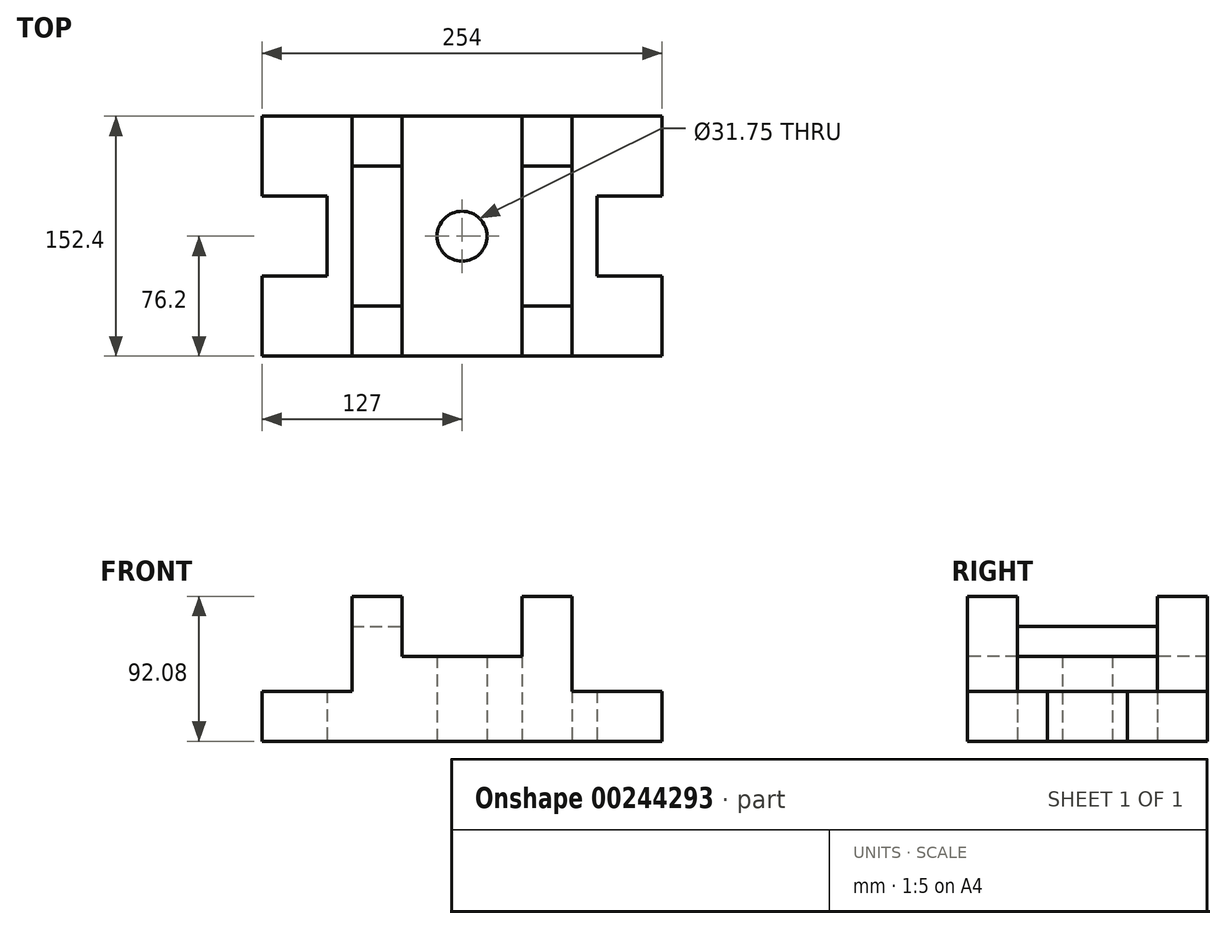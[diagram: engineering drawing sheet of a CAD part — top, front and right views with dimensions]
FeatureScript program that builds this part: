
annotation { "Feature Type Name" : "Feature", "Feature Type Description" : "" }
export const myFeature = defineFeature(function(context is Context, id is Id, definition is map)
    precondition{}
    {
        {
            var Q0;
            Q0=qCreatedBy(makeId("Top.planeOp"),FACE);
            var sketch = newSketch(context, id + "F0", { "sketchPlane" : qUnion([Q0])});
            skCircle(sketch, "E0", {"center": v(0, 0) * mm, "radius": 15.87 * mm});
            skLineSegment(sketch, "E1", {"start": v(0, 0) * mm, "end": v(0, 76.2) * mm});
            skLineSegment(sketch, "E2", {"start": v(0, 0) * mm, "end": v(0, -76.2) * mm});
            skLineSegment(sketch, "E3", {"start": v(0, 76.2) * mm, "end": v(38.1, 76.2) * mm});
            skLineSegment(sketch, "E4", {"start": v(0, -76.2) * mm, "end": v(38.1, -76.2) * mm});
            skLineSegment(sketch, "E5", {"start": v(38.1, 76.2) * mm, "end": v(38.1, -76.2) * mm});
            skLineSegment(sketch, "E6", {"start": v(38.1, 76.2) * mm, "end": v(69.85, 76.2) * mm});
            skLineSegment(sketch, "E7", {"start": v(69.85, 76.2) * mm, "end": v(69.85, 44.45) * mm});
            skLineSegment(sketch, "E8", {"start": v(69.85, 44.45) * mm, "end": v(38.1, 44.45) * mm});
            skLineSegment(sketch, "E9", {"start": v(38.1, -76.2) * mm, "end": v(69.85, -76.2) * mm});
            skLineSegment(sketch, "E10", {"start": v(69.85, -76.2) * mm, "end": v(69.85, -44.45) * mm});
            skLineSegment(sketch, "E11", {"start": v(69.85, -44.45) * mm, "end": v(38.1, -44.45) * mm});
            skLineSegment(sketch, "E12", {"start": v(69.85, 44.45) * mm, "end": v(69.85, -44.45) * mm});
            skLineSegment(sketch, "E13", {"start": v(69.85, 76.2) * mm, "end": v(127, 76.2) * mm});
            skLineSegment(sketch, "E14", {"start": v(127, 76.2) * mm, "end": v(127, 25.4) * mm});
            skLineSegment(sketch, "E15", {"start": v(127, 25.4) * mm, "end": v(85.72, 25.4) * mm});
            skLineSegment(sketch, "E16", {"start": v(85.72, 25.4) * mm, "end": v(85.72, -25.4) * mm});
            skLineSegment(sketch, "E17", {"start": v(85.72, -25.4) * mm, "end": v(127, -25.4) * mm});
            skLineSegment(sketch, "E18", {"start": v(127, -25.4) * mm, "end": v(127, -76.2) * mm});
            skLineSegment(sketch, "E19", {"start": v(127, -76.2) * mm, "end": v(69.85, -76.2) * mm});
            skLineSegment(sketch, "E20.MirrorCS", {"start": v(-85.72, 25.4) * mm, "end": v(-85.72, -25.4) * mm});
            skLineSegment(sketch, "E21.MirrorCS", {"start": v(-127, -25.4) * mm, "end": v(-127, -76.2) * mm});
            skLineSegment(sketch, "E22.MirrorCS", {"start": v(-127, -76.2) * mm, "end": v(-69.85, -76.2) * mm});
            skLineSegment(sketch, "E23.MirrorCS", {"start": v(-69.85, 44.45) * mm, "end": v(-69.85, -44.45) * mm});
            skLineSegment(sketch, "E24.MirrorCS", {"start": v(-69.85, 76.2) * mm, "end": v(-127, 76.2) * mm});
            skLineSegment(sketch, "E25.MirrorCS", {"start": v(-85.72, -25.4) * mm, "end": v(-127, -25.4) * mm});
            skLineSegment(sketch, "E26.MirrorCS", {"start": v(-69.85, -44.45) * mm, "end": v(-38.1, -44.45) * mm});
            skLineSegment(sketch, "E27.MirrorCS", {"start": v(-69.85, -76.2) * mm, "end": v(-69.85, -44.45) * mm});
            skLineSegment(sketch, "E28.MirrorCS", {"start": v(-38.1, -76.2) * mm, "end": v(-69.85, -76.2) * mm});
            skLineSegment(sketch, "E29.MirrorCS", {"start": v(-69.85, 44.45) * mm, "end": v(-38.1, 44.45) * mm});
            skLineSegment(sketch, "E30.MirrorCS", {"start": v(-69.85, 76.2) * mm, "end": v(-69.85, 44.45) * mm});
            skLineSegment(sketch, "E31.MirrorCS", {"start": v(-38.1, 76.2) * mm, "end": v(-69.85, 76.2) * mm});
            skLineSegment(sketch, "E32.MirrorCS", {"start": v(0, 76.2) * mm, "end": v(-38.1, 76.2) * mm});
            skLineSegment(sketch, "E33.MirrorCS", {"start": v(-38.1, 76.2) * mm, "end": v(-38.1, -76.2) * mm});
            skLineSegment(sketch, "E34.MirrorCS", {"start": v(-127, 76.2) * mm, "end": v(-127, 25.4) * mm});
            skLineSegment(sketch, "E35.MirrorCS", {"start": v(0, -76.2) * mm, "end": v(-38.1, -76.2) * mm});
            skLineSegment(sketch, "E36.MirrorCS", {"start": v(-127, 25.4) * mm, "end": v(-85.72, 25.4) * mm});
            skLineSegment(sketch, "E37.right", {"start": v(-38.1, 44.45) * mm, "end": v(-38.1, -44.45) * mm});
            skLineSegment(sketch, "E38.bottom", {"start": v(38.1, 44.45) * mm, "end": v(69.85, 44.45) * mm});
            skLineSegment(sketch, "E38.top", {"start": v(38.1, -44.45) * mm, "end": v(69.85, -44.45) * mm});
            skLineSegment(sketch, "E38.left", {"start": v(38.1, 44.45) * mm, "end": v(38.1, -44.45) * mm});
            skSolve(sketch);
        }
        {
            var Q0;
            Q0=makeQuery(id+"F0.imprint","IMPRINT",FACE,{"disambiguationData":[TD([[makeQuery(id+"F0.imprint","IMPRINT",EDGE,{"derivedFrom":sQuery(id+"F0.wireOp",EDGE,"E20.MirrorCS")}),1.0]])]});
            var Q1;
            Q1=makeQuery(id+"F0.imprint","IMPRINT",FACE,{"disambiguationData":[TD([[makeQuery(id+"F0.imprint","IMPRINT",EDGE,{"derivedFrom":sQuery(id+"F0.wireOp",EDGE,"E7")}),1.0]])]});
            extrude(context, id + "F1", {"entities" : qUnion([Q0, Q1]), "depth" : 31.75 * mm});
        }
        {
            var Q0;
            Q0=makeQuery(id+"F0.imprint","IMPRINT",FACE,{"disambiguationData":[TD([[makeQuery(id+"F0.imprint","IMPRINT",EDGE,{"derivedFrom":sQuery(id+"F0.wireOp",EDGE,"E27.MirrorCS")}),-1.0]])]});
            var Q1;
            {var subQ0=sQuery(id+"F0.wireOp",EDGE,"E6");Q1=makeQuery(id+"F0.imprint","IMPRINT",FACE,{"disambiguationData":[TD([[makeQuery(id+"F0.imprint","IMPRINT",EDGE,{"derivedFrom":subQ0}),-1.0]])]});}
            var Q2;
            {var subQ0=sQuery(id+"F0.wireOp",EDGE,"E9");Q2=makeQuery(id+"F0.imprint","IMPRINT",FACE,{"disambiguationData":[TD([[makeQuery(id+"F0.imprint","IMPRINT",EDGE,{"derivedFrom":subQ0}),1.0]])]});}
            var Q3;
            Q3=makeQuery(id+"F0.imprint","IMPRINT",FACE,{"disambiguationData":[TD([[makeQuery(id+"F0.imprint","IMPRINT",EDGE,{"derivedFrom":sQuery(id+"F0.wireOp",EDGE,"E30.MirrorCS")}),1.0]])]});
            extrude(context, id + "F2", {"entities" : qUnion([Q0, Q1, Q2, Q3]), "operationType" : NewBodyOperationType.ADD, "depth" : 92.07 * mm});
        }
        {
            var Q0;
            Q0=makeQuery(id+"F0.imprint","IMPRINT",FACE,{"disambiguationData":[TD([[makeQuery(id+"F0.imprint","IMPRINT",EDGE,{"derivedFrom":sQuery(id+"F0.wireOp",EDGE,"E29.MirrorCS")}),-1.0]])]});
            var Q1;
            Q1=makeQuery(id+"F0.imprint","IMPRINT",FACE,{"disambiguationData":[TD([[makeQuery(id+"F0.imprint","IMPRINT",EDGE,{"derivedFrom":sQuery(id+"F0.wireOp",EDGE,"E38.bottom")}),-1.0]])]});
            extrude(context, id + "F3", {"entities" : qUnion([Q0, Q1]), "operationType" : NewBodyOperationType.ADD, "depth" : 73.02 * mm});
        }
        {
            var Q0;
            {var subQ3=sQuery(id+"F0.wireOp",EDGE,"E3");Q0=makeQuery(id+"F0.imprint","IMPRINT",FACE,{"disambiguationData":[TD([[makeQuery(id+"F0.imprint","IMPRINT",EDGE,{"derivedFrom":subQ3}),-1.0]])]});}
            var Q1;
            {var subQ0=sQuery(id+"F0.wireOp",EDGE,"E32.MirrorCS");Q1=makeQuery(id+"F0.imprint","IMPRINT",FACE,{"disambiguationData":[TD([[makeQuery(id+"F0.imprint","IMPRINT",EDGE,{"derivedFrom":subQ0}),1.0]])]});}
            extrude(context, id + "F4", {"entities" : qUnion([Q0, Q1]), "operationType" : NewBodyOperationType.ADD, "depth" : 53.97 * mm});
        }
    });
